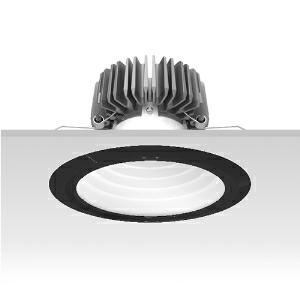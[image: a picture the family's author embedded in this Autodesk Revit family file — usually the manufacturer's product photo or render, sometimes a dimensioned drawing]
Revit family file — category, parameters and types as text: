
# Revit family: 3f_filippi_-_3f_reno_bianco_ampio_3f_filippi_-_30633_a01026_-_3f_reno_200_wh_3000-930_wide___vt_bk_01ae
name_source: partatom
category: Lighting Fixtures
units: mm (PartAtom-declared; Revit-internal decimal feet)

## family parameters
Cut with Voids When Loaded = No
Host = Face
Light Source = No
Part Type = Normal
Room Calculation Point = No
Round Connector Dimension = Use Diameter
Shared = No

## types (1)
- 3F Filippi - 3F Reno Bianco Ampio (1 x LED, 2537 lm, 37 W, 3000 K)
    Apparent Load = 37 VA
    Approval mark = CE
    CIE Flux Codes = 75 94 99 100 100
    Color Rendering = 90
    Color Temperature = 3000 K
    Control Gear = Electronic ballast
    Default Elevation = 1800 mm
    Description = ILLUMINOTECHNICAL
Luminous efficiency 100% (DLOR 100%, ULOR 0%).
Initial luminous flux of the luminaire 2537 lm.
Direct symmetric wide distribution.
Installation Interdistance Transv.D = 1.56 x hu - Long.D = 1.56 x hu.
Tabular UGR (CIE 117 - 4H-8H; S=0.25H; 70/50/20): RUG 21.8 - 21.7.
Beam angle: 74° - 74°.
Luminous efficacy 69 lm/W.
Lifetime (L90/B10): 30000 h. (tq+25°C)
Lifetime (L85/B10): 50000 h. (tq+25°C)
Lifetime (L70/B10): 80000 h. (tq+25°C)
Sudden decreased luminous flux after 50000 hours: 0% (C0).
Photobiological safety in compliance with IEC/TR 62778: RG0 risk exempt, (IEC 62471).
In compliance with IEC/EN 62722-2-1 - IEC/EN 62717 standards.

SOURCE
Compact LED module 3000/930.
Energy efficiency class (UE 2019/2020 - UE 2019/2015): E.
CIE 13.3 Colour rendering index: CRI >90 (R9 >50%).
IES TM-30 Fidelity Index: Rf = 92 Rg = 101.
CCT nominal colour temperature 3000 K.
Colour initial tolerance (MacAdam): SDCM 3.
Zhaga Book 3 compliant.

MECHANICAL
Passive heat dissipator in die-casting aluminium, oversized, for optimum thermal management of the LED module.
Parabolic element with graduated/concentric rings in white polycarbonate.
Transparent external lens with glossy and satin differentiated surfaces, with a cooling and anti-insect system in methacrylate (PMMA).
Fastening spring clips in stainless steel.
Dimensions: diameter 226 mm, height 146 mm. Weight 1.705 kg.
IP44 protection degree for exposed part, IP20 for recessed part.
Mechanical strength to impacts IK06 (1 joule).
Glow-wire test resistance 650°C.

ELECTRICAL
Wiring on a separate unit.
Halogen Free electronic wiring 230V-50/60Hz, power factor 0.95, THD <25%, constant output current, SELV, class II, 1 driver.
Power of the luminaire 37 W.
ENEC - CE.
SAFE FLICKER: PstLM=<1 and SVM=<0.4 (IEC TR 61547-1 and IEC TR 63158), to ensure a more comfortable and safe light.
Luminaire compliant with EN 60598-2-22 for power supply from a centralised emergency system CPSS (Central Power Supply System), not incorporated in the luminaire - high risk areas excluded. The default power and flux are 100% in AC and 100% in DC.
Ambient temperature from 0°C to +25°C.
Temperature class T6 max 85°C.
Relative humidity UR: <85%.

INSTALLATION
Pull-up recessed fitting.
False ceiling carving: 200 mm.
All accessories dedicated to this product are available on the Catalog and on our website www.3F-Filippi.com.

ACCESSORIES
A01026 - VT transparent glass, tempered, not flammable, locked and in line with the trim, in black polycarbonate.

APPLICATIONS
Environments: architectural, commercial, exhibition areas, transit areas, corridors, shops, display windows, service areas.
In false ceilings with narrow voids.

WARNING
Luminaire designed for disposal/recycling at end-of-life.
Replaceable (LED only) light source by a professional. Replaceable control gear by a professional.
    Height = 0 mm  [stored 0 ft]
    Lamp = 1 x LED
    Lamp Light Flux = 2537 lm
    Lamp Power = 37 W
    Lamp count = 1
    Length = 226 mm
    Lifetime = 50000 h
    Luminous efficacy = 69 lm/W
    Manufacturer = 3F Filippi
    ModVariant = No
    Model = 3F Filippi - 30633+A01026 - 3F Reno 200 WH 3000-930 WIDE + VT BK
    Mounting Place = Ceiling
    Mounting Type = Recessed
    Number of Poles = 1
    OnlyDefault = Yes
    Power Factor = 1
    Product Name = 3F Filippi - 3F Reno Bianco Ampio
    Product group = recessed luminaire
    ProductGroupID = 4
    Protection Class = Protection class II
    Protection Degree = IP 20
    RLX_Detail_Level = 1
    RLX_Emergency_Light_Flux = 0 lm
    RLX_Emergency_Type = 0
    RLX_Emergency_Type_DB = No
    RlxData = <blob elided: 100161 chars, md5=1a9935e8>
    Socket = socket
    Standby Power = 0 W
    System Light Flux = 2537 lm
    System Power = 37 W
    Type Comments = Product without accessories
    Type Image = 3ffilippi_3f_reno_200_wh__a01026.jpg
    URL = http://relux.com
    VarID = ---
    Voltage = 0 V
    Weight = 0.00 kg
    Width = 0 mm  [stored 0 ft]

note: [stored X ft] marks values corroborated as IEEE doubles in the binary element streams (Revit-internal decimal feet)

## geometry (parser evidence)
native form markers: Blend x4, Sweep x11
no freeform markers — native parametric forms only
